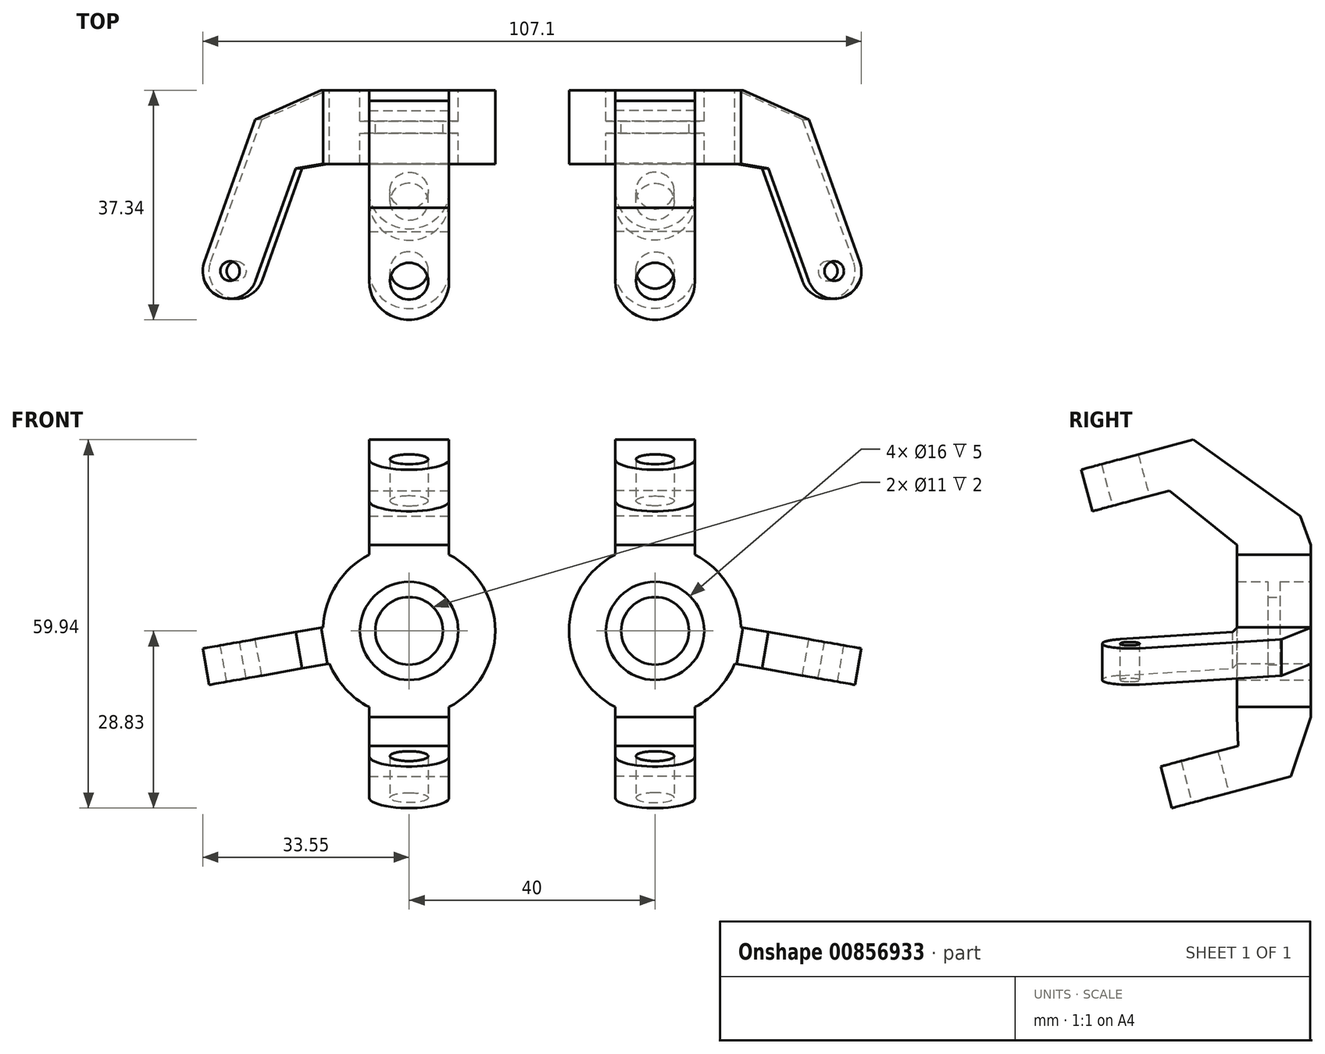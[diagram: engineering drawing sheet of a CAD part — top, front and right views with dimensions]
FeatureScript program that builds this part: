
annotation { "Feature Type Name" : "Feature", "Feature Type Description" : "" }
export const myFeature = defineFeature(function(context is Context, id is Id, definition is map)
    precondition{}
    {
        {
            var Q0;
            Q0=qCreatedBy(makeId("Front.planeOp"),FACE);
            var sketch = newSketch(context, id + "F0", { "sketchPlane" : qUnion([Q0])});
            skCircle(sketch, "E0", {"center": v(0, 0) * mm, "radius": 14 * mm});
            skSolve(sketch);
        }
        {
            var Q0;
            Q0 = qSketchRegion(id + "F0", true);
            extrude(context, id + "F1", {"entities" : qUnion([Q0]), "depth" : 12 * mm, "offsetDistance" : 25 * mm});
        }
        {
            var Q0;
            Q0=qCreatedBy(makeId("Right.planeOp"),FACE);
            var sketch = newSketch(context, id + "F2", { "sketchPlane" : qUnion([Q0])});
            skLineSegment(sketch, "E1", {"start": v(0, 0) * mm, "end": v(0, -88) * mm, "construction": true});
            skLineSegment(sketch, "E2", {"start": v(0, -88) * mm, "end": v(-29.25, 21.15) * mm, "construction": true});
            skLineSegment(sketch, "E3", {"start": v(-24.4, -22.07) * mm, "end": v(-18.12, -20.39) * mm, "construction": true});
            skLineSegment(sketch, "E4", {"start": v(-35.53, 19.47) * mm, "end": v(-29.25, 21.15) * mm, "construction": true});
            skLineSegment(sketch, "E5", {"start": v(-35.53, 19.47) * mm, "end": v(-37.34, 26.23) * mm});
            skLineSegment(sketch, "E6", {"start": v(-37.34, 26.23) * mm, "end": v(-19.1, 31.11) * mm});
            skLineSegment(sketch, "E7", {"start": v(-19.1, 31.11) * mm, "end": v(0, 14) * mm, "construction": true});
            skLineSegment(sketch, "E8", {"start": v(-12, 14) * mm, "end": v(-22.97, 22.83) * mm});
            skLineSegment(sketch, "E9", {"start": v(-22.97, 22.83) * mm, "end": v(-35.53, 19.47) * mm});
            skLineSegment(sketch, "E10", {"start": v(-24.4, -22.07) * mm, "end": v(-22.58, -28.83) * mm});
            skLineSegment(sketch, "E11", {"start": v(-22.58, -28.83) * mm, "end": v(-3.27, -23.65) * mm});
            skLineSegment(sketch, "E12", {"start": v(-3.27, -23.65) * mm, "end": v(0, -14) * mm});
            skLineSegment(sketch, "E13", {"start": v(-12, -14) * mm, "end": v(-11.84, -18.7) * mm});
            skLineSegment(sketch, "E14", {"start": v(-11.84, -18.7) * mm, "end": v(-24.4, -22.07) * mm});
            skLineSegment(sketch, "E15", {"start": v(0, -14) * mm, "end": v(-12, -14) * mm, "construction": true});
            skLineSegment(sketch, "E16", {"start": v(0, 14) * mm, "end": v(-12, 14) * mm, "construction": true});
            skLineSegment(sketch, "E17", {"start": v(-11.84, -18.7) * mm, "end": v(-3.27, -23.65) * mm, "construction": true});
            skLineSegment(sketch, "E18", {"start": v(-7.55, -21.18) * mm, "end": v(-23.49, -25.45) * mm, "construction": true});
            skLineSegment(sketch, "E19", {"start": v(-19.1, 31.11) * mm, "end": v(-22.97, 22.83) * mm, "construction": true});
            skLineSegment(sketch, "E20", {"start": v(-21.04, 26.97) * mm, "end": v(-36.43, 22.85) * mm, "construction": true});
            skLineSegment(sketch, "E21", {"start": v(-21.04, 26.97) * mm, "end": v(-6, 14) * mm, "construction": true});
            skLineSegment(sketch, "E22", {"start": v(-6, 14) * mm, "end": v(-6, -14) * mm, "construction": true});
            skLineSegment(sketch, "E23", {"start": v(-6, -14) * mm, "end": v(-7.55, -21.18) * mm, "construction": true});
            skLineSegment(sketch, "E24.0", {"start": v(0, -14) * mm, "end": v(0, 14) * mm});
            skLineSegment(sketch, "E25.0", {"start": v(-12, -14) * mm, "end": v(-12, 14) * mm});
            skLineSegment(sketch, "E26", {"start": v(-19.1, 31.11) * mm, "end": v(-1.71, 18.7) * mm});
            skLineSegment(sketch, "E27", {"start": v(-1.71, 18.7) * mm, "end": v(0, 14) * mm});
            skSolve(sketch);
        }
        {
            var Q0;
            Q0 = qSketchRegion(id + "F2", true);
            extrude(context, id + "F3", {"entities" : qUnion([Q0]), "operationType" : NewBodyOperationType.ADD, "oppositeDirection" : true, "depth" : 13 * mm, "offsetDistance" : 25 * mm, "symmetric" : true});
        }
        {
            var Q0;
            Q0=makeQuery(id+"F3.opExtrude","CAP_EDGE",EDGE,{"disambiguationData":[OSD([sQuery(id+"F2.wireOp",EDGE,"E5")])],"isStart":false});
            var Q1;
            Q1=makeQuery(id+"F3.opExtrude","CAP_EDGE",EDGE,{"disambiguationData":[OSD([sQuery(id+"F2.wireOp",EDGE,"E5")])],"isStart":true});
            var Q2;
            Q2=makeQuery(id+"F3.opExtrude","CAP_EDGE",EDGE,{"disambiguationData":[OSD([sQuery(id+"F2.wireOp",EDGE,"E10")])],"isStart":false});
            var Q3;
            Q3=makeQuery(id+"F3.opExtrude","CAP_EDGE",EDGE,{"disambiguationData":[OSD([sQuery(id+"F2.wireOp",EDGE,"E10")])],"isStart":true});
            fillet(context, id + "F4", {"entities" : qUnion([Q0, Q1, Q2, Q3]), "radius" : 6.5 * mm, "tangentPropagation" : true, "allowEdgeOverflow" : false});
        }
        {
            var Q0;
            Q0=makeQuery(id+"F3.opExtrude","SWEPT_FACE",FACE,{"disambiguationData":[OSD([sQuery(id+"F2.wireOp",EDGE,"E11")])]});
            var sketch = newSketch(context, id + "F5", { "sketchPlane" : qUnion([Q0])});
            skCircle(sketch, "E28", {"center": v(0, 22.78) * mm, "radius": 3.1 * mm});
            skSolve(sketch);
        }
        {
            var Q0;
            Q0 = qSketchRegion(id + "F5", true);
            extrude(context, id + "F6", {"entities" : qUnion([Q0]), "operationType" : NewBodyOperationType.REMOVE, "endBound" : BoundingType.THROUGH_ALL, "oppositeDirection" : true, "depth" : 25 * mm, "offsetDistance" : 25 * mm});
        }
        {
            var Q0;
            Q0=qCreatedBy(makeId("Top.planeOp"),FACE);
            var sketch = newSketch(context, id + "F7", { "sketchPlane" : qUnion([Q0])});
            skLineSegment(sketch, "E29", {"start": v(0, 0) * mm, "end": v(0, -59.2) * mm, "construction": true});
            skSolve(sketch);
        }
        {
            var Q0;
            Q0=sQuery(id+"F7.wireOp",EDGE,"E29");
            var Q1;
            Q1=qCreatedBy(makeId("Top.planeOp"),FACE);
            cPlane(context, id + "F8", {"entities" : qUnion([Q0, Q1]), "cplaneType" : CPlaneType.LINE_ANGLE, "offset" : 15 * mm, "angle" : 10 * degree, "width" : 150 * mm, "height" : 150 * mm});
        }
        {
            var Q0;
            Q0=qCreatedBy(id+"F8.planeOp",FACE);
            var sketch = newSketch(context, id + "F9", { "sketchPlane" : qUnion([Q0])});
            skArc(sketch, "E30", {"start": v(-24.81, 30.95) * mm, "mid": v(-30.58, 33.64) * mm, "end": v(-33.27, 27.87) * mm});
            skCircle(sketch, "E31", {"center": v(-29.04, 29.4) * mm, "radius": 1.6 * mm});
            skLineSegment(sketch, "E32", {"start": v(-29.04, 29.4) * mm, "end": v(-21.52, 8.74) * mm, "construction": true});
            skLineSegment(sketch, "E33", {"start": v(-24.81, 30.95) * mm, "end": v(-33.27, 27.87) * mm, "construction": true});
            skLineSegment(sketch, "E34", {"start": v(-24.81, 30.95) * mm, "end": v(-18.18, 12.72) * mm});
            skLineSegment(sketch, "E35", {"start": v(-14, 6) * mm, "end": v(-21.52, 8.74) * mm, "construction": true});
            skLineSegment(sketch, "E36", {"start": v(-14, 12) * mm, "end": v(-18.18, 12.72) * mm});
            skLineSegment(sketch, "E37", {"start": v(-33.27, 27.87) * mm, "end": v(-24.86, 4.76) * mm});
            skLineSegment(sketch, "E38", {"start": v(-24.86, 4.76) * mm, "end": v(-14, 0) * mm});
            skLineSegment(sketch, "E39", {"start": v(-18.18, 12.72) * mm, "end": v(-24.86, 4.76) * mm, "construction": true});
            skLineSegment(sketch, "E40", {"start": v(-3.97, 0) * mm, "end": v(-3.97, 12) * mm});
            skLineSegment(sketch, "E41", {"start": v(-3.97, 0) * mm, "end": v(-14, 0) * mm});
            skLineSegment(sketch, "E42", {"start": v(-3.97, 12) * mm, "end": v(-14, 12) * mm});
            skLineSegment(sketch, "E43", {"start": v(-14, 0) * mm, "end": v(-14, 12) * mm, "construction": true});
            skSolve(sketch);
        }
        {
            var Q0;
            Q0 = qSketchRegion(id + "F9", true);
            extrude(context, id + "F10", {"entities" : qUnion([Q0]), "operationType" : NewBodyOperationType.ADD, "depth" : 6 * mm, "offsetDistance" : 25 * mm, "symmetric" : true});
        }
        {
            var Q0;
            Q0=qCreatedBy(makeId("Right.planeOp"),FACE);
            var sketch = newSketch(context, id + "F11", { "sketchPlane" : qUnion([Q0])});
            skLineSegment(sketch, "E44", {"start": v(0, 8) * mm, "end": v(-5, 8) * mm});
            skLineSegment(sketch, "E45", {"start": v(-5, 8) * mm, "end": v(-5, 5.5) * mm});
            skLineSegment(sketch, "E46", {"start": v(-5, 5.5) * mm, "end": v(-7, 5.5) * mm});
            skLineSegment(sketch, "E47", {"start": v(-7, 5.5) * mm, "end": v(-7, 8) * mm});
            skLineSegment(sketch, "E48", {"start": v(-7, 8) * mm, "end": v(-12, 8) * mm});
            skLineSegment(sketch, "E49", {"start": v(0, 0) * mm, "end": v(-12, 0) * mm});
            skLineSegment(sketch, "E50", {"start": v(0, 0) * mm, "end": v(0, 8) * mm});
            skLineSegment(sketch, "E51.0", {"start": v(-12, 0) * mm, "end": v(-12, 8) * mm});
            skPoint(sketch, "E52.orphan", {"position": v(-12, 14) * mm});
            skPoint(sketch, "E53.orphan", {"position": v(-12, -14) * mm});
            skLineSegment(sketch, "E54", {"start": v(0, 0) * mm, "end": v(5.22, 0) * mm, "construction": true});
            skSolve(sketch);
        }
        {
            var Q0;
            Q0 = qSketchRegion(id + "F11", true);
            var Q1;
            Q1=sQuery(id+"F11.wireOp",EDGE,"E54");
            revolve(context, id + "F12", {"operationType" : NewBodyOperationType.REMOVE, "surfaceOperationType" : NewSurfaceOperationType.NEW, "entities" : qUnion([Q0]), "axis" : qUnion([Q1]), "revolveType" : RevolveType.FULL, "oppositeDirection" : true});
        }
        {
            var Q0;
            Q0=qCreatedBy(makeId("Right.planeOp"),FACE);
            cPlane(context, id + "F13", {"entities" : qUnion([Q0]), "cplaneType" : CPlaneType.OFFSET, "offset" : 20 * mm, "width" : 150 * mm, "height" : 150 * mm});
        }
        {
            var Q0;
            Q0=makeQuery(id+"F1.opExtrude","SWEPT_BODY",BODY,{"disambiguationData":[OSD([sQuery(id+"F0.wireOp",EDGE,"E0")])]});
            var Q1;
            Q1=qCreatedBy(id+"F13.planeOp",FACE);
            mirror(context, id + "F14", {"entities" : qUnion([Q0]), "mirrorPlane" : qUnion([Q1])});
        }
    });
